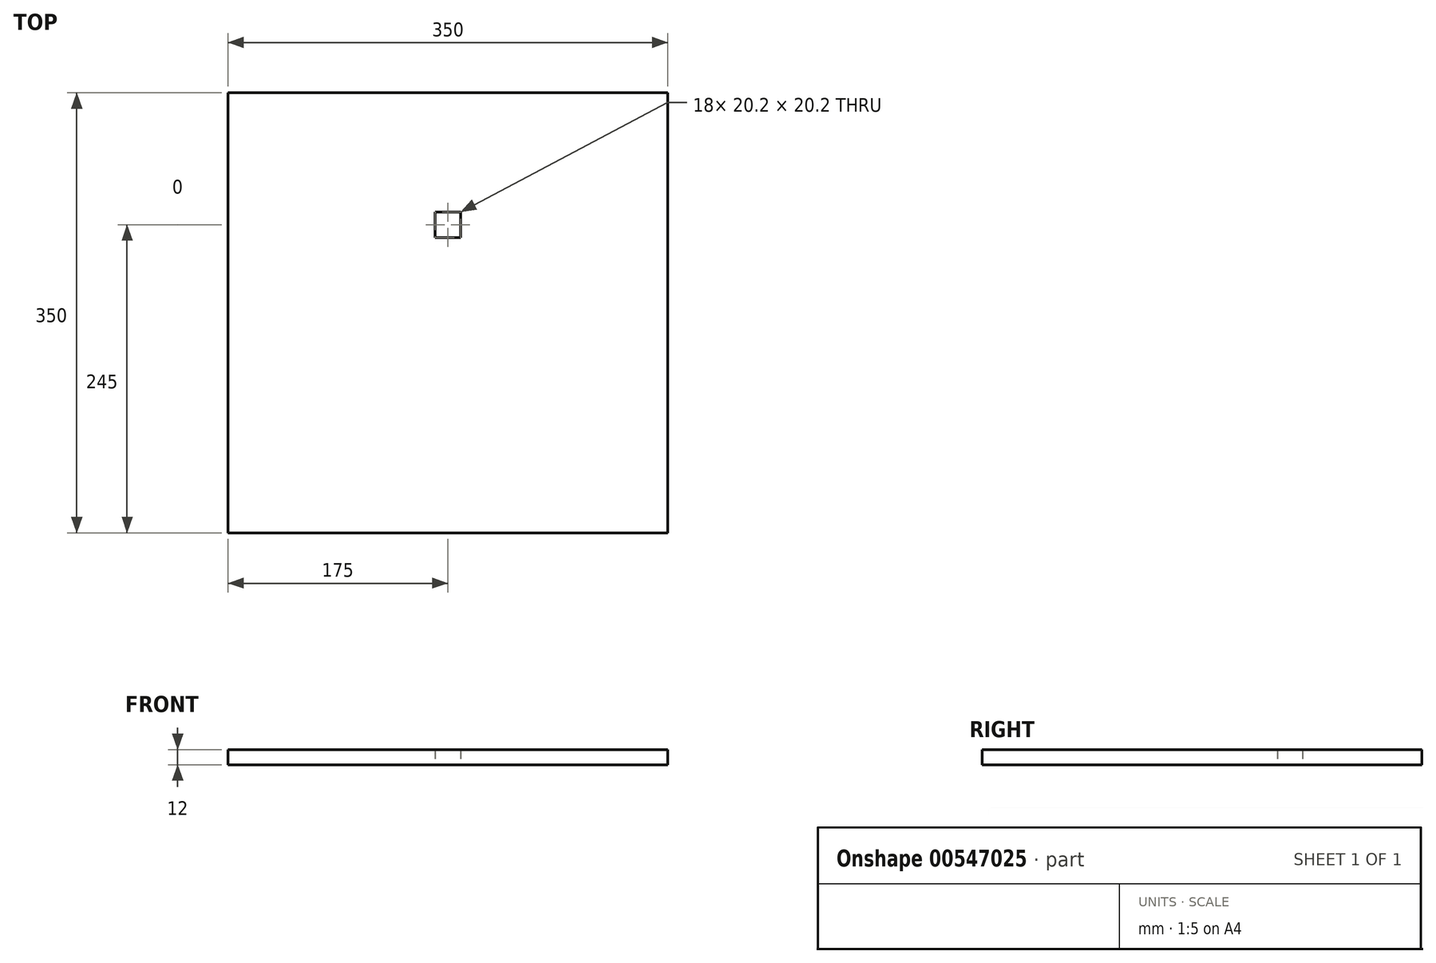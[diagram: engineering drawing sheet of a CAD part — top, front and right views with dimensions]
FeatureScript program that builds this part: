
annotation { "Feature Type Name" : "Feature", "Feature Type Description" : "" }
export const myFeature = defineFeature(function(context is Context, id is Id, definition is map)
    precondition{}
    {
        {
            var Q0;
            Q0=qCreatedBy(makeId("Top.planeOp"),FACE);
            var sketch = newSketch(context, id + "F0", { "sketchPlane" : qUnion([Q0])});
            skLineSegment(sketch, "E0.bottom", {"start": v(-175, -175) * mm, "end": v(175, -175) * mm});
            skLineSegment(sketch, "E0.top", {"start": v(-175, 175) * mm, "end": v(175, 175) * mm});
            skLineSegment(sketch, "E0.left", {"start": v(-175, -175) * mm, "end": v(-175, 175) * mm});
            skLineSegment(sketch, "E0.right", {"start": v(175, -175) * mm, "end": v(175, 175) * mm});
            skLineSegment(sketch, "E1.bottom", {"start": v(-10.1, 80.1) * mm, "end": v(10.1, 80.1) * mm});
            skLineSegment(sketch, "E1.top", {"start": v(-10.1, 59.9) * mm, "end": v(10.1, 59.9) * mm});
            skLineSegment(sketch, "E1.left", {"start": v(-10.1, 80.1) * mm, "end": v(-10.1, 59.9) * mm});
            skLineSegment(sketch, "E1.right", {"start": v(10.1, 80.1) * mm, "end": v(10.1, 59.9) * mm});
            skPoint(sketch, "E1.middle", {"position": v(0, 70) * mm});
            skSolve(sketch);
        }
        {
            var Q0;
            Q0 = qSketchRegion(id + "F0", true);
            extrude(context, id + "F1", {"entities" : qUnion([Q0]), "depth" : 12 * mm, "offsetDistance" : 25 * mm});
        }
    });
